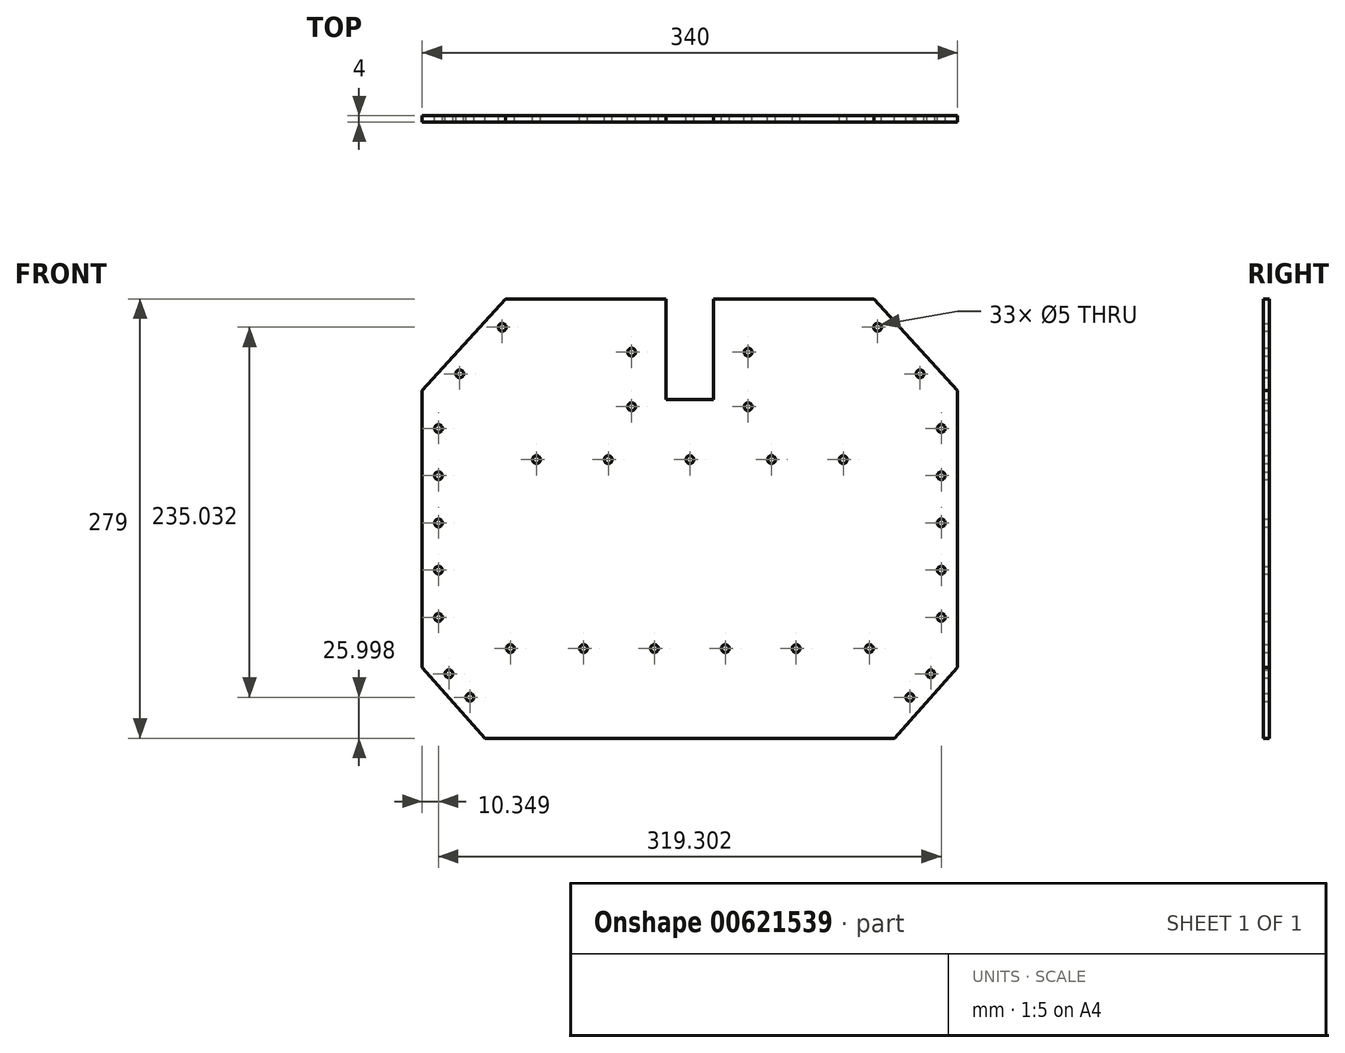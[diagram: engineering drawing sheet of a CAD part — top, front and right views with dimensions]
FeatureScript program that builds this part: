
annotation { "Feature Type Name" : "Feature", "Feature Type Description" : "" }
export const myFeature = defineFeature(function(context is Context, id is Id, definition is map)
    precondition{}
    {
        {
            var Q0;
            Q0=qCreatedBy(makeId("Front.planeOp"),FACE);
            var sketch = newSketch(context, id + "F0", { "sketchPlane" : qUnion([Q0])});
            skLineSegment(sketch, "E0.bottom", {"start": v(-15, -6) * mm, "end": v(15, -6) * mm});
            skLineSegment(sketch, "E0.left", {"start": v(-170, -6) * mm, "end": v(-170, -176) * mm});
            skLineSegment(sketch, "E0.right", {"start": v(170, -6) * mm, "end": v(170, -176) * mm});
            skLineSegment(sketch, "E1", {"start": v(-130, -221) * mm, "end": v(130, -221) * mm});
            skLineSegment(sketch, "E2", {"start": v(-170, -176) * mm, "end": v(-130, -221) * mm});
            skLineSegment(sketch, "E3", {"start": v(170, -176) * mm, "end": v(130, -221) * mm});
            skLineSegment(sketch, "E4.left", {"start": v(-15, -6) * mm, "end": v(-15, 58) * mm});
            skLineSegment(sketch, "E4.right", {"start": v(15, -6) * mm, "end": v(15, 58) * mm});
            skLineSegment(sketch, "E5", {"start": v(-117, 58) * mm, "end": v(-15, 58) * mm});
            skLineSegment(sketch, "E6", {"start": v(-117, 58) * mm, "end": v(-170, 0) * mm});
            skLineSegment(sketch, "E7", {"start": v(117, 58) * mm, "end": v(170, 0) * mm});
            skLineSegment(sketch, "E8", {"start": v(-170, 0) * mm, "end": v(-170, -6) * mm});
            skLineSegment(sketch, "E9", {"start": v(170, 0) * mm, "end": v(170, -6) * mm});
            skLineSegment(sketch, "E10.trimOffspring", {"start": v(15, 58) * mm, "end": v(117, 58) * mm});
            skPoint(sketch, "E11.orphan", {"position": v(0, 396.25) * mm});
            skPoint(sketch, "E12", {"position": v(-119.18, 40.03) * mm});
            skPoint(sketch, "E13", {"position": v(-146.16, 10.5) * mm});
            skPoint(sketch, "E14", {"position": v(-159.65, -24.26) * mm});
            skPoint(sketch, "E15", {"position": v(-159.65, -54.26) * mm});
            skPoint(sketch, "E16", {"position": v(-159.65, -84.26) * mm});
            skPoint(sketch, "E17", {"position": v(-159.65, -114.26) * mm});
            skPoint(sketch, "E18", {"position": v(-159.65, -144.26) * mm});
            skPoint(sketch, "E19", {"position": v(-153, -180.05) * mm});
            skPoint(sketch, "E20", {"position": v(-139.72, -195) * mm});
            skPoint(sketch, "E21", {"position": v(37, 24.24) * mm});
            skPoint(sketch, "E22", {"position": v(37, -10.43) * mm});
            skPoint(sketch, "E23", {"position": v(-37, 24.24) * mm});
            skPoint(sketch, "E24", {"position": v(-37, -10.43) * mm});
            skPoint(sketch, "E25", {"position": v(-97.4, -44) * mm});
            skPoint(sketch, "E26", {"position": v(-51.84, -44) * mm});
            skPoint(sketch, "E27", {"position": v(0, -44) * mm});
            skPoint(sketch, "E28", {"position": v(51.84, -44) * mm});
            skPoint(sketch, "E29", {"position": v(97.4, -44) * mm});
            skPoint(sketch, "E30", {"position": v(119.18, 40.03) * mm});
            skPoint(sketch, "E31", {"position": v(146.16, 10.5) * mm});
            skPoint(sketch, "E32", {"position": v(159.65, -24.26) * mm});
            skPoint(sketch, "E33", {"position": v(159.65, -54.26) * mm});
            skPoint(sketch, "E34", {"position": v(159.65, -84.26) * mm});
            skPoint(sketch, "E35", {"position": v(159.65, -114.26) * mm});
            skPoint(sketch, "E36", {"position": v(159.65, -144.26) * mm});
            skPoint(sketch, "E37", {"position": v(153, -180.05) * mm});
            skPoint(sketch, "E38", {"position": v(139.72, -195) * mm});
            skPoint(sketch, "E39", {"position": v(-67.5, -164) * mm});
            skPoint(sketch, "E40", {"position": v(-22.5, -164) * mm});
            skPoint(sketch, "E41", {"position": v(22.5, -164) * mm});
            skPoint(sketch, "E42", {"position": v(67.5, -164) * mm});
            skPoint(sketch, "E43.orphan", {"position": v(-114, -164) * mm});
            skPoint(sketch, "E44.end.orphan", {"position": v(114, -164) * mm});
            skCircle(sketch, "E45", {"center": v(-97.4, -44) * mm, "radius": 2.5 * mm});
            skCircle(sketch, "E46", {"center": v(-119.18, 40.03) * mm, "radius": 2.5 * mm});
            skCircle(sketch, "E47", {"center": v(-146.16, 10.5) * mm, "radius": 2.5 * mm});
            skCircle(sketch, "E48", {"center": v(-159.65, -24.26) * mm, "radius": 2.5 * mm});
            skCircle(sketch, "E49", {"center": v(-159.65, -54.26) * mm, "radius": 2.5 * mm});
            skCircle(sketch, "E50", {"center": v(-159.65, -84.26) * mm, "radius": 2.5 * mm});
            skCircle(sketch, "E51", {"center": v(-159.65, -114.26) * mm, "radius": 2.5 * mm});
            skCircle(sketch, "E52", {"center": v(-159.65, -144.26) * mm, "radius": 2.5 * mm});
            skCircle(sketch, "E53", {"center": v(-153, -180.05) * mm, "radius": 2.5 * mm});
            skCircle(sketch, "E54", {"center": v(-139.72, -195) * mm, "radius": 2.5 * mm});
            skCircle(sketch, "E55", {"center": v(-114, -164) * mm, "radius": 2.5 * mm});
            skCircle(sketch, "E56", {"center": v(-67.5, -164) * mm, "radius": 2.5 * mm});
            skCircle(sketch, "E57", {"center": v(-22.5, -164) * mm, "radius": 2.5 * mm});
            skCircle(sketch, "E58", {"center": v(22.5, -164) * mm, "radius": 2.5 * mm});
            skCircle(sketch, "E59", {"center": v(67.5, -164) * mm, "radius": 2.5 * mm});
            skCircle(sketch, "E60", {"center": v(114, -164) * mm, "radius": 2.5 * mm});
            skCircle(sketch, "E61", {"center": v(139.72, -195) * mm, "radius": 2.5 * mm});
            skCircle(sketch, "E62", {"center": v(153, -180.05) * mm, "radius": 2.5 * mm});
            skCircle(sketch, "E63", {"center": v(159.65, -144.26) * mm, "radius": 2.5 * mm});
            skCircle(sketch, "E64", {"center": v(159.65, -114.26) * mm, "radius": 2.5 * mm});
            skCircle(sketch, "E65", {"center": v(159.65, -84.26) * mm, "radius": 2.5 * mm});
            skCircle(sketch, "E66", {"center": v(159.65, -54.26) * mm, "radius": 2.5 * mm});
            skCircle(sketch, "E67", {"center": v(159.65, -24.26) * mm, "radius": 2.5 * mm});
            skCircle(sketch, "E68", {"center": v(146.16, 10.5) * mm, "radius": 2.5 * mm});
            skCircle(sketch, "E69", {"center": v(119.18, 40.03) * mm, "radius": 2.5 * mm});
            skCircle(sketch, "E70", {"center": v(37, 24.24) * mm, "radius": 2.5 * mm});
            skCircle(sketch, "E71", {"center": v(-37, 24.24) * mm, "radius": 2.5 * mm});
            skCircle(sketch, "E72", {"center": v(-37, -10.43) * mm, "radius": 2.5 * mm});
            skCircle(sketch, "E73", {"center": v(-51.84, -44) * mm, "radius": 2.5 * mm});
            skCircle(sketch, "E74", {"center": v(0, -44) * mm, "radius": 2.5 * mm});
            skCircle(sketch, "E75", {"center": v(51.84, -44) * mm, "radius": 2.5 * mm});
            skCircle(sketch, "E76", {"center": v(97.4, -44) * mm, "radius": 2.5 * mm});
            skCircle(sketch, "E77", {"center": v(37, -10.43) * mm, "radius": 2.5 * mm});
            skSolve(sketch);
        }
        {
            var Q0;
            Q0=makeQuery(id+"F0.imprint","IMPRINT",FACE,{"disambiguationData":[TD([[makeQuery(id+"F0.imprint","IMPRINT",EDGE,{"derivedFrom":sQuery(id+"F0.wireOp",EDGE,"E0.left")}),1.0]])]});
            extrude(context, id + "F1", {"entities" : qUnion([Q0]), "depth" : 4 * mm, "offsetDistance" : 25 * mm});
        }
    });
